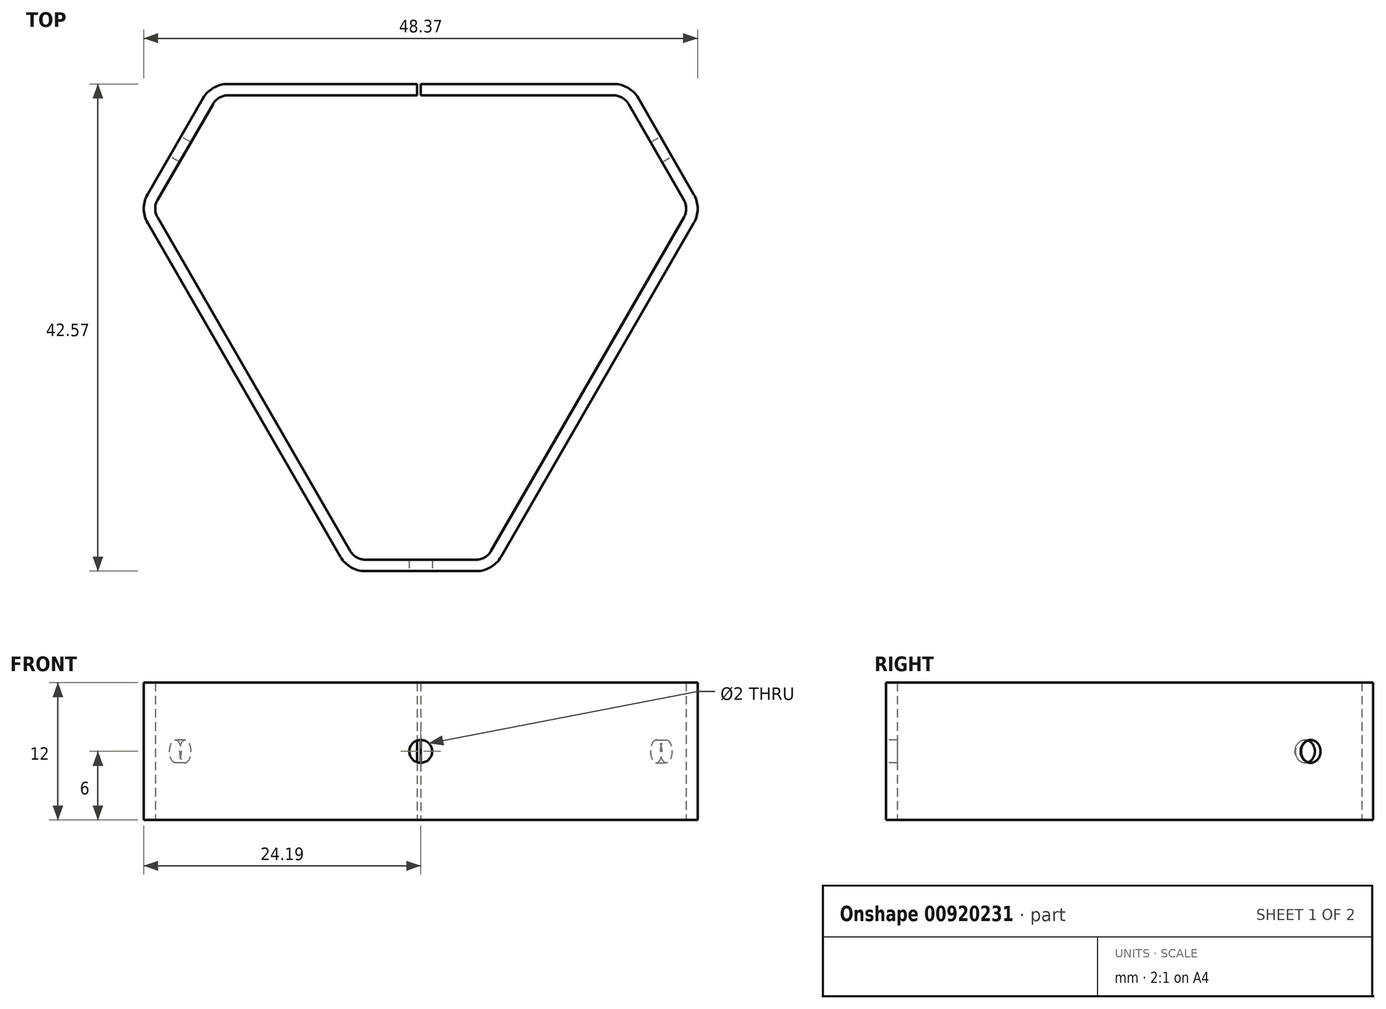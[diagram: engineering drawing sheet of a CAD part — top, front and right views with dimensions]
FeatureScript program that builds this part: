
annotation { "Feature Type Name" : "Feature", "Feature Type Description" : "" }
export const myFeature = defineFeature(function(context is Context, id is Id, definition is map)
    precondition{}
    {
        {
            var Q0;
            Q0=qCreatedBy(makeId("Top.planeOp"),FACE);
            var sketch = newSketch(context, id + "F0", { "sketchPlane" : qUnion([Q0])});
            skLineSegment(sketch, "E0.0", {"start": v(23.42, 5.92) * mm, "end": v(6.58, -23.25) * mm});
            skLineSegment(sketch, "E0.1", {"start": v(-6.58, -23.25) * mm, "end": v(-23.42, 5.93) * mm});
            skLineSegment(sketch, "E0.2", {"start": v(-16.85, 17.32) * mm, "end": v(-0.32, 17.32) * mm});
            skLineSegment(sketch, "E1", {"start": v(-21, 12.12) * mm, "end": v(-21.63, 12.49) * mm, "construction": true});
            skLineSegment(sketch, "E2", {"start": v(-18.58, 16.32) * mm, "end": v(-23.42, 7.93) * mm});
            skLineSegment(sketch, "E3", {"start": v(18.58, 16.32) * mm, "end": v(23.42, 7.92) * mm});
            skPoint(sketch, "E4.orphan", {"position": v(0, -34.64) * mm});
            skPoint(sketch, "E5", {"position": v(0.27, 17.32) * mm});
            skPoint(sketch, "E6", {"position": v(-0.32, 17.32) * mm});
            skLineSegment(sketch, "E7.trimOffspring", {"start": v(0.27, 17.32) * mm, "end": v(16.85, 17.32) * mm});
            skPoint(sketch, "E8.orphan", {"position": v(30, 17.32) * mm});
            skPoint(sketch, "E9.start.orphan", {"position": v(0, -24.25) * mm});
            skLineSegment(sketch, "E10", {"start": v(-4.85, -24.25) * mm, "end": v(4.85, -24.25) * mm});
            skLineSegment(sketch, "E11", {"start": v(0.27, 17.32) * mm, "end": v(0, 17.32) * mm});
            skCircle(sketch, "E12", {"center": v(0, 0) * mm, "radius": 34.64 * mm, "construction": true});
            skCircle(sketch, "E13", {"center": v(0, 0) * mm, "radius": 24.97 * mm, "construction": true});
            skLineSegment(sketch, "E14", {"start": v(30, 17.32) * mm, "end": v(0, -34.64) * mm, "construction": true});
            skLineSegment(sketch, "E15", {"start": v(0, -34.64) * mm, "end": v(-30, 17.32) * mm, "construction": true});
            skLineSegment(sketch, "E16", {"start": v(-30, 17.32) * mm, "end": v(30, 17.32) * mm, "construction": true});
            skPoint(sketch, "E17.visualSharp", {"position": v(24, 6.92) * mm});
            skArc(sketch, "E17.filletArc", {"start": v(23.42, 5.92) * mm, "mid": v(23.68, 6.92) * mm, "end": v(23.42, 7.92) * mm});
            skPoint(sketch, "E18.visualSharp", {"position": v(18, 17.32) * mm});
            skArc(sketch, "E18.filletArc", {"start": v(18.58, 16.32) * mm, "mid": v(17.85, 17.05) * mm, "end": v(16.85, 17.32) * mm});
            skPoint(sketch, "E19.visualSharp", {"position": v(6, -24.25) * mm});
            skArc(sketch, "E19.filletArc", {"start": v(4.85, -24.25) * mm, "mid": v(5.85, -23.98) * mm, "end": v(6.58, -23.25) * mm});
            skPoint(sketch, "E20.visualSharp", {"position": v(-6, -24.25) * mm});
            skArc(sketch, "E20.filletArc", {"start": v(-6.58, -23.25) * mm, "mid": v(-5.85, -23.98) * mm, "end": v(-4.85, -24.25) * mm});
            skPoint(sketch, "E21.visualSharp", {"position": v(-24, 6.93) * mm});
            skArc(sketch, "E21.filletArc", {"start": v(-23.42, 7.93) * mm, "mid": v(-23.7, 6.93) * mm, "end": v(-23.42, 5.93) * mm});
            skPoint(sketch, "E22.visualSharp", {"position": v(-18, 17.32) * mm});
            skArc(sketch, "E22.filletArc", {"start": v(-16.85, 17.32) * mm, "mid": v(-17.85, 17.05) * mm, "end": v(-18.58, 16.32) * mm});
            skSolve(sketch);
        }
        {
            var Q0;
            Q0=qCreatedBy(makeId("Right.planeOp"),FACE);
            var sketch = newSketch(context, id + "F1", { "sketchPlane" : qUnion([Q0])});
            skLineSegment(sketch, "E23.bottom", {"start": v(16.82, 6) * mm, "end": v(17.82, 6) * mm});
            skLineSegment(sketch, "E23.top", {"start": v(16.82, -6) * mm, "end": v(17.82, -6) * mm});
            skLineSegment(sketch, "E23.left", {"start": v(16.82, 6) * mm, "end": v(16.82, -6) * mm});
            skLineSegment(sketch, "E23.right", {"start": v(17.82, 6) * mm, "end": v(17.82, -6) * mm});
            skPoint(sketch, "E23.middle", {"position": v(17.32, 0) * mm});
            skSolve(sketch);
        }
        {
            var Q0;
            Q0=makeQuery(id+"F1.imprint","IMPRINT",FACE,{"disambiguationData":[TD([[makeQuery(id+"F1.imprint","IMPRINT",EDGE,{"derivedFrom":sQuery(id+"F1.wireOp",EDGE,"E23.bottom")}),-1.0]])]});
            var Q1;
            Q1 = qConstructionFilter(qBodyType(qCreatedBy(id + "F0" ,EDGE), BodyType.WIRE), ConstructionObject.NO);
            sweep(context, id + "F2", {"profiles" : qUnion([Q0]), "path" : qUnion([Q1])});
        }
        {
            var Q0;
            Q0=makeQuery(id+"F2.opSweep","SWEPT_FACE",FACE,{"disambiguationData":[OSD([sQuery(id+"F0.wireOp",EDGE,"E10"),sQuery(id+"F1.wireOp",EDGE,"E23.right")])]});
            var sketch = newSketch(context, id + "F3", { "sketchPlane" : qUnion([Q0])});
            skCircle(sketch, "E24", {"center": v(0, 0) * mm, "radius": 1 * mm});
            skSolve(sketch);
        }
        {
            var Q0;
            Q0=makeQuery(id+"F3.imprint","IMPRINT",FACE,{"disambiguationData":[TD([[makeQuery(id+"F3.imprint","IMPRINT",EDGE,{"derivedFrom":sQuery(id+"F3.wireOp",EDGE,"E24")}),1.0]])]});
            extrude(context, id + "F4", {"entities" : qUnion([Q0]), "operationType" : NewBodyOperationType.REMOVE, "endBound" : BoundingType.UP_TO_NEXT, "oppositeDirection" : true, "depth" : 25 * mm, "offsetDistance" : 25 * mm});
        }
        {
            var Q0;
            Q0=makeQuery(id+"F2.opSweep","SWEPT_FACE",FACE,{"disambiguationData":[OSD([sQuery(id+"F0.wireOp",EDGE,"E3"),sQuery(id+"F1.wireOp",EDGE,"E23.right")])]});
            var sketch = newSketch(context, id + "F5", { "sketchPlane" : qUnion([Q0])});
            skCircle(sketch, "E25", {"center": v(0, 0) * mm, "radius": 1 * mm});
            skSolve(sketch);
        }
        {
            var Q0;
            Q0=makeQuery(id+"F5.imprint","IMPRINT",FACE,{"disambiguationData":[TD([[makeQuery(id+"F5.imprint","IMPRINT",EDGE,{"derivedFrom":sQuery(id+"F5.wireOp",EDGE,"E25")}),1.0]])]});
            extrude(context, id + "F6", {"entities" : qUnion([Q0]), "operationType" : NewBodyOperationType.REMOVE, "endBound" : BoundingType.UP_TO_NEXT, "oppositeDirection" : true, "depth" : 25 * mm, "offsetDistance" : 25 * mm});
        }
        {
            var Q0;
            Q0=makeQuery(id+"F2.opSweep","SWEPT_FACE",FACE,{"disambiguationData":[OSD([sQuery(id+"F0.wireOp",EDGE,"E2"),sQuery(id+"F1.wireOp",EDGE,"E23.right")])]});
            var sketch = newSketch(context, id + "F7", { "sketchPlane" : qUnion([Q0])});
            skCircle(sketch, "E26", {"center": v(0, 0) * mm, "radius": 1 * mm});
            skSolve(sketch);
        }
        {
            var Q0;
            Q0 = qSketchRegion(id + "F7", true);
            extrude(context, id + "F8", {"entities" : qUnion([Q0]), "operationType" : NewBodyOperationType.REMOVE, "endBound" : BoundingType.UP_TO_NEXT, "oppositeDirection" : true, "depth" : 25 * mm, "offsetDistance" : 25 * mm});
        }
    });
